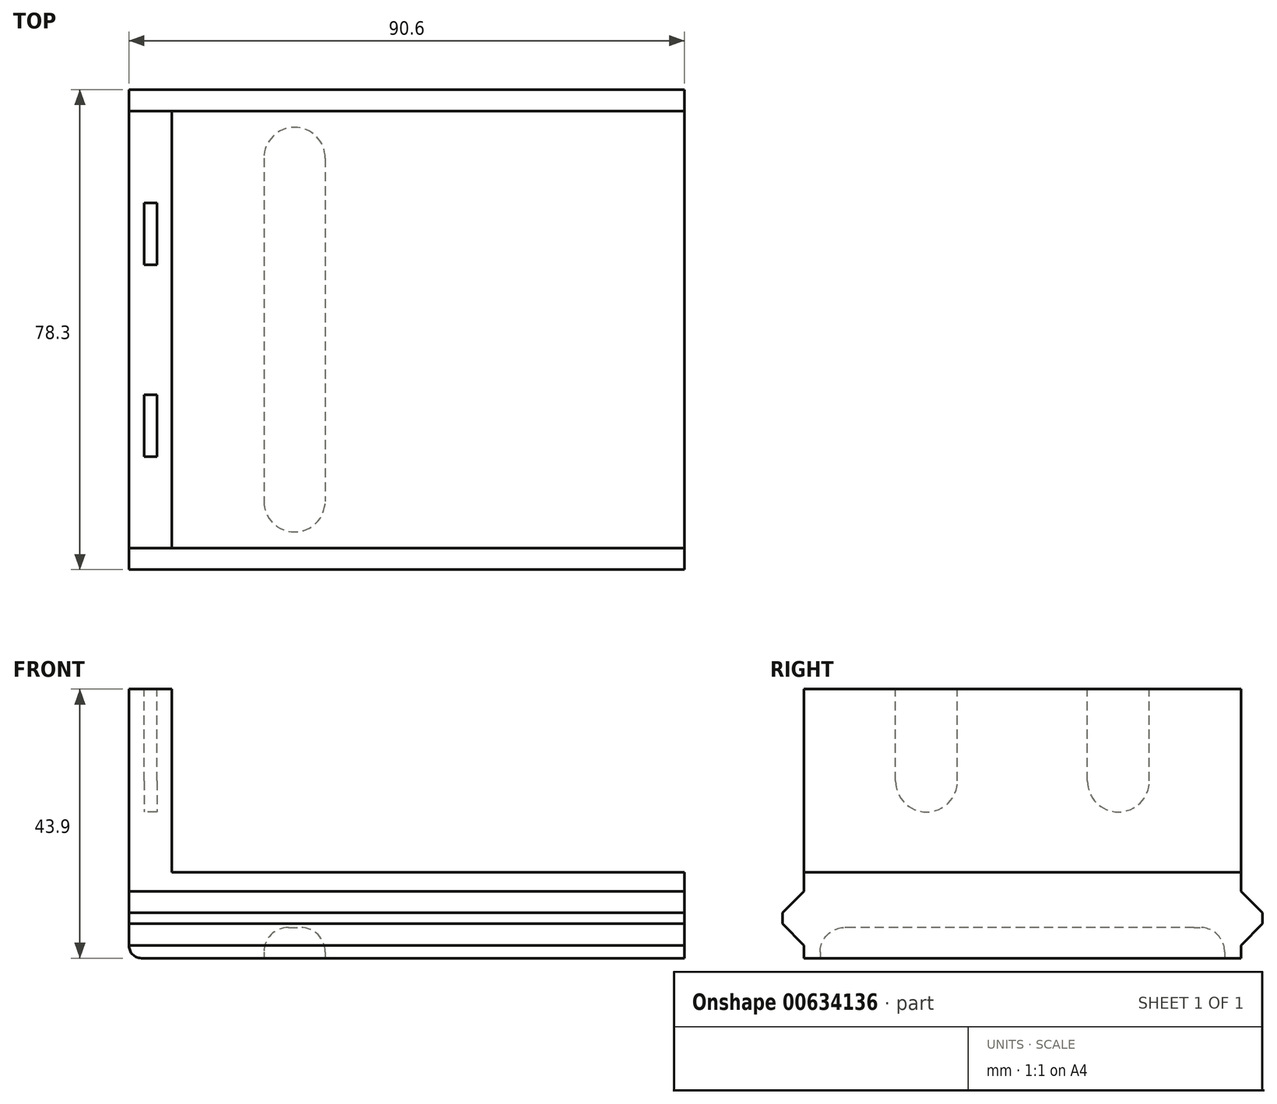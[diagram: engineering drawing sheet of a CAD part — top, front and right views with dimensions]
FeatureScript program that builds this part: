
annotation { "Feature Type Name" : "Feature", "Feature Type Description" : "" }
export const myFeature = defineFeature(function(context is Context, id is Id, definition is map)
    precondition{}
    {
        {
            var Q0;
            Q0=qCreatedBy(makeId("Top.planeOp"),FACE);
            var sketch = newSketch(context, id + "F0", { "sketchPlane" : qUnion([Q0])});
            skLineSegment(sketch, "E0.bottom", {"start": v(-45.3, 35.65) * mm, "end": v(45.3, 35.65) * mm});
            skLineSegment(sketch, "E0.top", {"start": v(-45.3, -35.65) * mm, "end": v(45.3, -35.65) * mm});
            skLineSegment(sketch, "E0.left", {"start": v(-45.3, 35.65) * mm, "end": v(-45.3, -35.65) * mm});
            skLineSegment(sketch, "E0.right", {"start": v(45.3, 35.65) * mm, "end": v(45.3, -35.65) * mm});
            skSolve(sketch);
        }
        {
            var Q0;
            Q0=makeQuery(id+"F0.imprint","IMPRINT",FACE,{"disambiguationData":[TD([[makeQuery(id+"F0.imprint","IMPRINT",EDGE,{"derivedFrom":sQuery(id+"F0.wireOp",EDGE,"E0.bottom")}),-1.0]])]});
            extrude(context, id + "F1", {"entities" : qUnion([Q0]), "depth" : 14 * mm, "offsetDistance" : 25 * mm});
        }
        {
            var Q0;
            Q0=makeQuery(id+"F1.opExtrude","CAP_FACE",FACE,{"disambiguationData":[OSD([sQuery(id+"F0.wireOp",EDGE,"E0.bottom"),sQuery(id+"F0.wireOp",EDGE,"E0.top"),sQuery(id+"F0.wireOp",EDGE,"E0.left"),sQuery(id+"F0.wireOp",EDGE,"E0.right")])],"isStart":false});
            var sketch = newSketch(context, id + "F2", { "sketchPlane" : qUnion([Q0])});
            skLineSegment(sketch, "E1.bottom", {"start": v(-45.3, 35.65) * mm, "end": v(-38.3, 35.65) * mm});
            skLineSegment(sketch, "E1.top", {"start": v(-45.3, -35.65) * mm, "end": v(-38.3, -35.65) * mm});
            skLineSegment(sketch, "E1.left", {"start": v(-45.3, 35.65) * mm, "end": v(-45.3, -35.65) * mm});
            skLineSegment(sketch, "E1.right", {"start": v(-38.3, 35.65) * mm, "end": v(-38.3, -35.65) * mm});
            skSolve(sketch);
        }
        {
            var Q0;
            Q0=makeQuery(id+"F2.imprint","IMPRINT",FACE,{"disambiguationData":[TD([[makeQuery(id+"F2.imprint","IMPRINT",EDGE,{"derivedFrom":sQuery(id+"F2.wireOp",EDGE,"E1.bottom")}),-1.0]])]});
            extrude(context, id + "F3", {"entities" : qUnion([Q0]), "operationType" : NewBodyOperationType.ADD, "depth" : 29.9 * mm, "offsetDistance" : 25 * mm});
        }
        {
            var Q0;
            Q0=makeQuery(id+"F1.opExtrude","SWEPT_FACE",FACE,{"disambiguationData":[OSD([sQuery(id+"F0.wireOp",EDGE,"E0.right")])]});
            var sketch = newSketch(context, id + "F4", { "sketchPlane" : qUnion([Q0])});
            skLineSegment(sketch, "E2", {"start": v(-35.65, 2.1) * mm, "end": v(-39.15, 5.6) * mm});
            skLineSegment(sketch, "E3", {"start": v(-39.15, 5.6) * mm, "end": v(-39.15, 7.4) * mm});
            skLineSegment(sketch, "E4", {"start": v(-39.15, 7.4) * mm, "end": v(-35.65, 10.9) * mm});
            skLineSegment(sketch, "E5", {"start": v(-35.65, 10.9) * mm, "end": v(-35.65, 2.1) * mm});
            skLineSegment(sketch, "E6", {"start": v(35.65, 10.9) * mm, "end": v(39.15, 7.4) * mm});
            skLineSegment(sketch, "E7", {"start": v(39.15, 7.4) * mm, "end": v(39.15, 5.6) * mm});
            skLineSegment(sketch, "E8", {"start": v(39.15, 5.6) * mm, "end": v(35.65, 2.1) * mm});
            skLineSegment(sketch, "E9", {"start": v(35.65, 2.1) * mm, "end": v(35.65, 10.9) * mm});
            skSolve(sketch);
        }
        {
            var Q0;
            Q0=makeQuery(id+"F4.imprint","IMPRINT",FACE,{"disambiguationData":[TD([[makeQuery(id+"F4.imprint","IMPRINT",EDGE,{"derivedFrom":sQuery(id+"F4.wireOp",EDGE,"E2")}),-1.0]])]});
            var Q1;
            Q1=makeQuery(id+"F4.imprint","IMPRINT",FACE,{"disambiguationData":[TD([[makeQuery(id+"F4.imprint","IMPRINT",EDGE,{"derivedFrom":sQuery(id+"F4.wireOp",EDGE,"E6")}),-1.0]])]});
            extrude(context, id + "F5", {"entities" : qUnion([Q0, Q1]), "depth" : -90.6 * mm, "offsetDistance" : 25 * mm});
        }
        {
            var Q0;
            Q0=makeQuery(id+"F5.opExtrude","SWEPT_BODY",BODY,{"disambiguationData":[OSD([sQuery(id+"F4.wireOp",EDGE,"E2"),sQuery(id+"F4.wireOp",EDGE,"E3"),sQuery(id+"F4.wireOp",EDGE,"E4"),sQuery(id+"F4.wireOp",EDGE,"E5")])]});
            var Q1;
            Q1=makeQuery(id+"F1.opExtrude","SWEPT_BODY",BODY,{"disambiguationData":[OSD([sQuery(id+"F0.wireOp",EDGE,"E0.bottom"),sQuery(id+"F0.wireOp",EDGE,"E0.top"),sQuery(id+"F0.wireOp",EDGE,"E0.left"),sQuery(id+"F0.wireOp",EDGE,"E0.right")])]});
            var Q2;
            Q2=makeQuery(id+"F5.opExtrude","SWEPT_BODY",BODY,{"disambiguationData":[OSD([sQuery(id+"F4.wireOp",EDGE,"E6"),sQuery(id+"F4.wireOp",EDGE,"E7"),sQuery(id+"F4.wireOp",EDGE,"E8"),sQuery(id+"F4.wireOp",EDGE,"E9")])]});
            booleanBodies(context, id + "F6", {"operationType" : BooleanOperationType.UNION, "tools" : qUnion([Q0, Q1, Q2])});
        }
        {
            var Q0;
            Q0=makeQuery(id+"F3.opExtrude","CAP_FACE",FACE,{"disambiguationData":[OSD([sQuery(id+"F2.wireOp",EDGE,"E1.bottom"),sQuery(id+"F2.wireOp",EDGE,"E1.top"),sQuery(id+"F2.wireOp",EDGE,"E1.left"),sQuery(id+"F2.wireOp",EDGE,"E1.right")])],"isStart":false});
            var sketch = newSketch(context, id + "F7", { "sketchPlane" : qUnion([Q0])});
            skLineSegment(sketch, "E10.bottom", {"start": v(-42.85, -20.7) * mm, "end": v(-40.75, -20.7) * mm});
            skLineSegment(sketch, "E10.top", {"start": v(-42.85, -10.6) * mm, "end": v(-40.75, -10.6) * mm});
            skLineSegment(sketch, "E10.left", {"start": v(-42.85, -20.7) * mm, "end": v(-42.85, -10.6) * mm});
            skLineSegment(sketch, "E10.right", {"start": v(-40.75, -20.7) * mm, "end": v(-40.75, -10.6) * mm});
            skLineSegment(sketch, "E11.bottom", {"start": v(-42.85, 10.6) * mm, "end": v(-40.75, 10.6) * mm});
            skLineSegment(sketch, "E11.top", {"start": v(-42.85, 20.7) * mm, "end": v(-40.75, 20.7) * mm});
            skLineSegment(sketch, "E11.left", {"start": v(-42.85, 10.6) * mm, "end": v(-42.85, 20.7) * mm});
            skLineSegment(sketch, "E11.right", {"start": v(-40.75, 10.6) * mm, "end": v(-40.75, 20.7) * mm});
            skSolve(sketch);
        }
        {
            var Q0;
            Q0=makeQuery(id+"F7.imprint","IMPRINT",FACE,{"disambiguationData":[TD([[makeQuery(id+"F7.imprint","IMPRINT",EDGE,{"derivedFrom":sQuery(id+"F7.wireOp",EDGE,"E10.bottom")}),1.0]])]});
            var Q1;
            Q1=makeQuery(id+"F7.imprint","IMPRINT",FACE,{"disambiguationData":[TD([[makeQuery(id+"F7.imprint","IMPRINT",EDGE,{"derivedFrom":sQuery(id+"F7.wireOp",EDGE,"E11.bottom")}),1.0]])]});
            extrude(context, id + "F8", {"entities" : qUnion([Q0, Q1]), "operationType" : NewBodyOperationType.REMOVE, "oppositeDirection" : true, "depth" : 20.05 * mm, "offsetDistance" : 25 * mm});
        }
        {
            var Q0;
            Q0=makeQuery(id+"F8.boolean.opBoolean","COPY",EDGE,{"derivedFrom":makeQuery(id+"F8.opExtrude","CAP_EDGE",EDGE,{"disambiguationData":[OSD([sQuery(id+"F7.wireOp",EDGE,"E10.bottom")])],"isStart":false})});
            var Q1;
            Q1=makeQuery(id+"F8.boolean.opBoolean","COPY",EDGE,{"derivedFrom":makeQuery(id+"F8.opExtrude","CAP_EDGE",EDGE,{"disambiguationData":[OSD([sQuery(id+"F7.wireOp",EDGE,"E10.top")])],"isStart":false})});
            var Q2;
            Q2=makeQuery(id+"F8.boolean.opBoolean","COPY",EDGE,{"derivedFrom":makeQuery(id+"F8.opExtrude","CAP_EDGE",EDGE,{"disambiguationData":[OSD([sQuery(id+"F7.wireOp",EDGE,"E11.top")])],"isStart":false})});
            var Q3;
            Q3=makeQuery(id+"F8.boolean.opBoolean","COPY",EDGE,{"derivedFrom":makeQuery(id+"F8.opExtrude","CAP_EDGE",EDGE,{"disambiguationData":[OSD([sQuery(id+"F7.wireOp",EDGE,"E11.bottom")])],"isStart":false})});
            fillet(context, id + "F9", {"entities" : qUnion([Q0, Q1, Q2, Q3]), "radius" : 5.05 * mm, "tangentPropagation" : true, "allowEdgeOverflow" : false});
        }
        {
            var Q0;
            Q0=makeQuery(id+"F1.opExtrude","CAP_EDGE",EDGE,{"disambiguationData":[OSD([sQuery(id+"F0.wireOp",EDGE,"E0.left")])],"isStart":true});
            fillet(context, id + "F10", {"entities" : qUnion([Q0]), "radius" : 2 * mm, "tangentPropagation" : true, "allowEdgeOverflow" : false});
        }
        {
            var Q0;
            Q0=makeQuery(id+"F1.opExtrude","CAP_FACE",FACE,{"disambiguationData":[OSD([sQuery(id+"F0.wireOp",EDGE,"E0.bottom"),sQuery(id+"F0.wireOp",EDGE,"E0.top"),sQuery(id+"F0.wireOp",EDGE,"E0.left"),sQuery(id+"F0.wireOp",EDGE,"E0.right")])],"isStart":true});
            var sketch = newSketch(context, id + "F11", { "sketchPlane" : qUnion([Q0])});
            skLineSegment(sketch, "E12", {"start": v(-23.3, -28) * mm, "end": v(-23.3, 28) * mm});
            skLineSegment(sketch, "E13", {"start": v(-13.3, -28) * mm, "end": v(-13.3, 28) * mm});
            skArc(sketch, "E14", {"start": v(-23.3, 28) * mm, "mid": v(-18.3, 33) * mm, "end": v(-13.3, 28) * mm});
            skArc(sketch, "E15", {"start": v(-23.3, -28) * mm, "mid": v(-18.3, -33) * mm, "end": v(-13.3, -28) * mm});
            skSolve(sketch);
        }
        {
            var Q0;
            Q0=makeQuery(id+"F11.imprint","IMPRINT",FACE,{"disambiguationData":[TD([[makeQuery(id+"F11.imprint","IMPRINT",EDGE,{"derivedFrom":sQuery(id+"F11.wireOp",EDGE,"E12")}),-1.0]])]});
            extrude(context, id + "F12", {"entities" : qUnion([Q0]), "operationType" : NewBodyOperationType.REMOVE, "oppositeDirection" : true, "depth" : 5 * mm, "offsetDistance" : 25 * mm});
        }
        {
            var Q0;
            Q0=makeQuery(id+"F12.boolean.opBoolean","COPY",FACE,{"derivedFrom":makeQuery(id+"F12.opExtrude","CAP_FACE",FACE,{"disambiguationData":[OSD([sQuery(id+"F11.wireOp",EDGE,"E12"),sQuery(id+"F11.wireOp",EDGE,"E13"),sQuery(id+"F11.wireOp",EDGE,"E14"),sQuery(id+"F11.wireOp",EDGE,"E15")])],"isStart":false})});
            fillet(context, id + "F13", {"entities" : qUnion([Q0]), "radius" : 4 * mm, "tangentPropagation" : true, "allowEdgeOverflow" : false});
        }
    });
